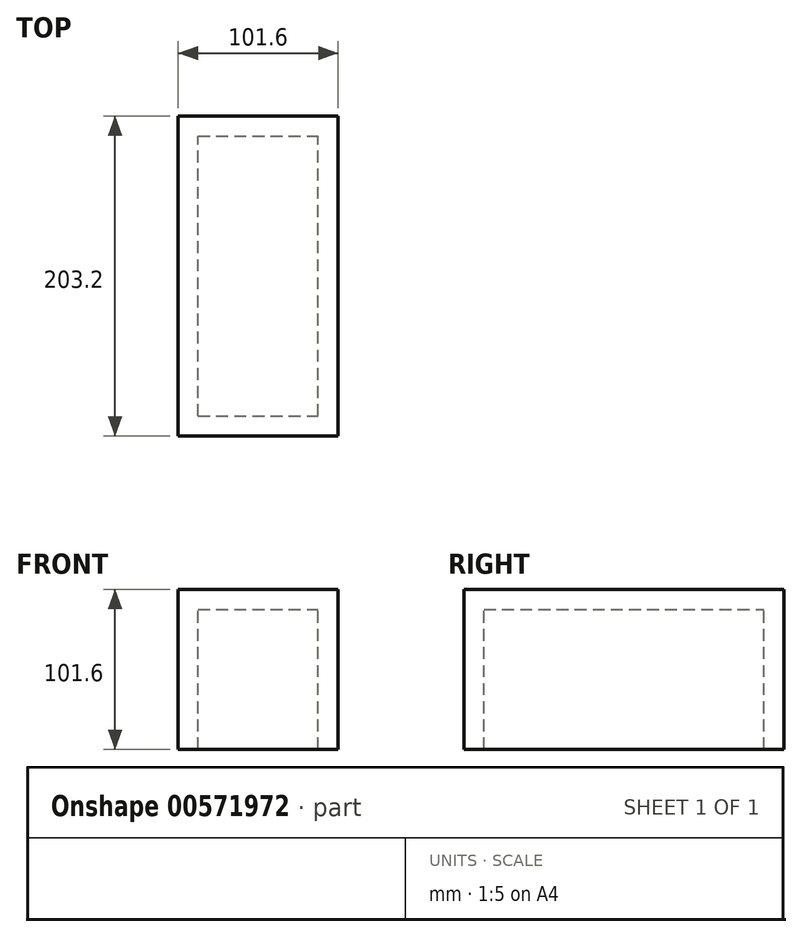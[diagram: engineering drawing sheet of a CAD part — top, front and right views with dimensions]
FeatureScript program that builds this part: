
annotation { "Feature Type Name" : "Feature", "Feature Type Description" : "" }
export const myFeature = defineFeature(function(context is Context, id is Id, definition is map)
    precondition{}
    {
        {
            var Q0;
            Q0=qCreatedBy(makeId("Front.planeOp"),FACE);
            var sketch = newSketch(context, id + "F0", { "sketchPlane" : qUnion([Q0])});
            skLineSegment(sketch, "E0.bottom", {"start": v(-50.8, -50.8) * mm, "end": v(50.8, -50.8) * mm});
            skLineSegment(sketch, "E0.top", {"start": v(-50.8, 50.8) * mm, "end": v(50.8, 50.8) * mm});
            skLineSegment(sketch, "E0.left", {"start": v(-50.8, -50.8) * mm, "end": v(-50.8, 50.8) * mm});
            skLineSegment(sketch, "E0.right", {"start": v(50.8, -50.8) * mm, "end": v(50.8, 50.8) * mm});
            skPoint(sketch, "E0.middle", {"position": v(0, 0) * mm});
            skSolve(sketch);
        }
        {
            var Q0;
            Q0 = qSketchRegion(id + "F0", true);
            extrude(context, id + "F1", {"entities" : qUnion([Q0]), "depth" : 203.2 * mm, "offsetDistance" : 25.4 * mm});
        }
        {
            var Q0;
            Q0=makeQuery(id+"F1.opExtrude","SWEPT_FACE",FACE,{"disambiguationData":[OSD([sQuery(id+"F0.wireOp",EDGE,"E0.bottom")])]});
            shell(context, id + "F2", {"entities" : qUnion([Q0]), "thickness" : 12.7 * mm});
        }
    });
